# Revit family: IEK_Выключатель_ОткрытойУстановки_10А IP54_ФОРС
name_source: partatom
category: Выключатели
units: mm (PartAtom-declared; Revit-internal decimal feet)

## family parameters
Всегда вертикально = Да
На основе рабочей плоскости = Нет
Общий = Нет
При загрузке вырезать с полостями = Нет
Размер круглого соединителя = Использовать диаметр
Сохранять ориентацию аннотаций = Да
Тип детали = Переключатель
Точка расчета площади = Нет

## types (2) — shared parameters
ADSK_URL страницы изделия = https://www.iek.ru
ADSK_Версия Revit = 2019
ADSK_Версия семейства = 1.0
ADSK_Группирование = III ЭЛЕКТРОУСТАНОВОЧНЫЕ И ЭЛЕКТРОМОНТАЖНЫЕ ИЗДЕЛИЯ
ADSK_Единица измерения = шт
ADSK_Завод-изготовитель = IEK
ADSK_Количество фаз = 1
ADSK_Количество фаз числовое = 1
ADSK_Марка = ФОРС
ADSK_Материал = Окраска - RAL 7035
ADSK_Материал наименование = Пластик
ADSK_Напряжение = 220 В
IEK_URL = https://www.iek.ru
IEK_Описание = Выключатели и розетки серии «ФОРС» IP54 для открытой установки предназначены для помещений с повышенной влажностью и запыленностью: подвалов, гаражей, мастерских. Дизайн розеток и выключателей данной серии идеально впишется в интерьер промышленных предприятий.
KSI_CMa_Строительные материалы = 01.7.14.03
KSI_CPr_Строительные изделия = 20.4.01
Высота = 92 мм
Глубина = 55 мм
Изготовитель = IEK
Материал крышки = RAL 9004
Степень защиты = IP54
Тип монтажа = Поверхность монтажа (открытая установка)
Ширина = 65 мм

## per-type parameters (varying)
| type | ADSK_Код изделия | ADSK_Масса | ADSK_Наименование | IEK_Цена за единицу |
| ВС20-1-0-ФСр | EVS10-K03-10-54-DC | 0.09 | Выключатель 1-клавишный для открытой установки ВС20-1-0-ФСр ФОРС IP54 IEK | 368.6 |
| ВСк20-1-0-ФСр | EVS13-K03-10-54-DC | 0.13 | Выключатель 1-клавишный для открытой установки кнопочный ВСк20-1-0-ФСр ФОРС IP54 IEK | 447.76 |
